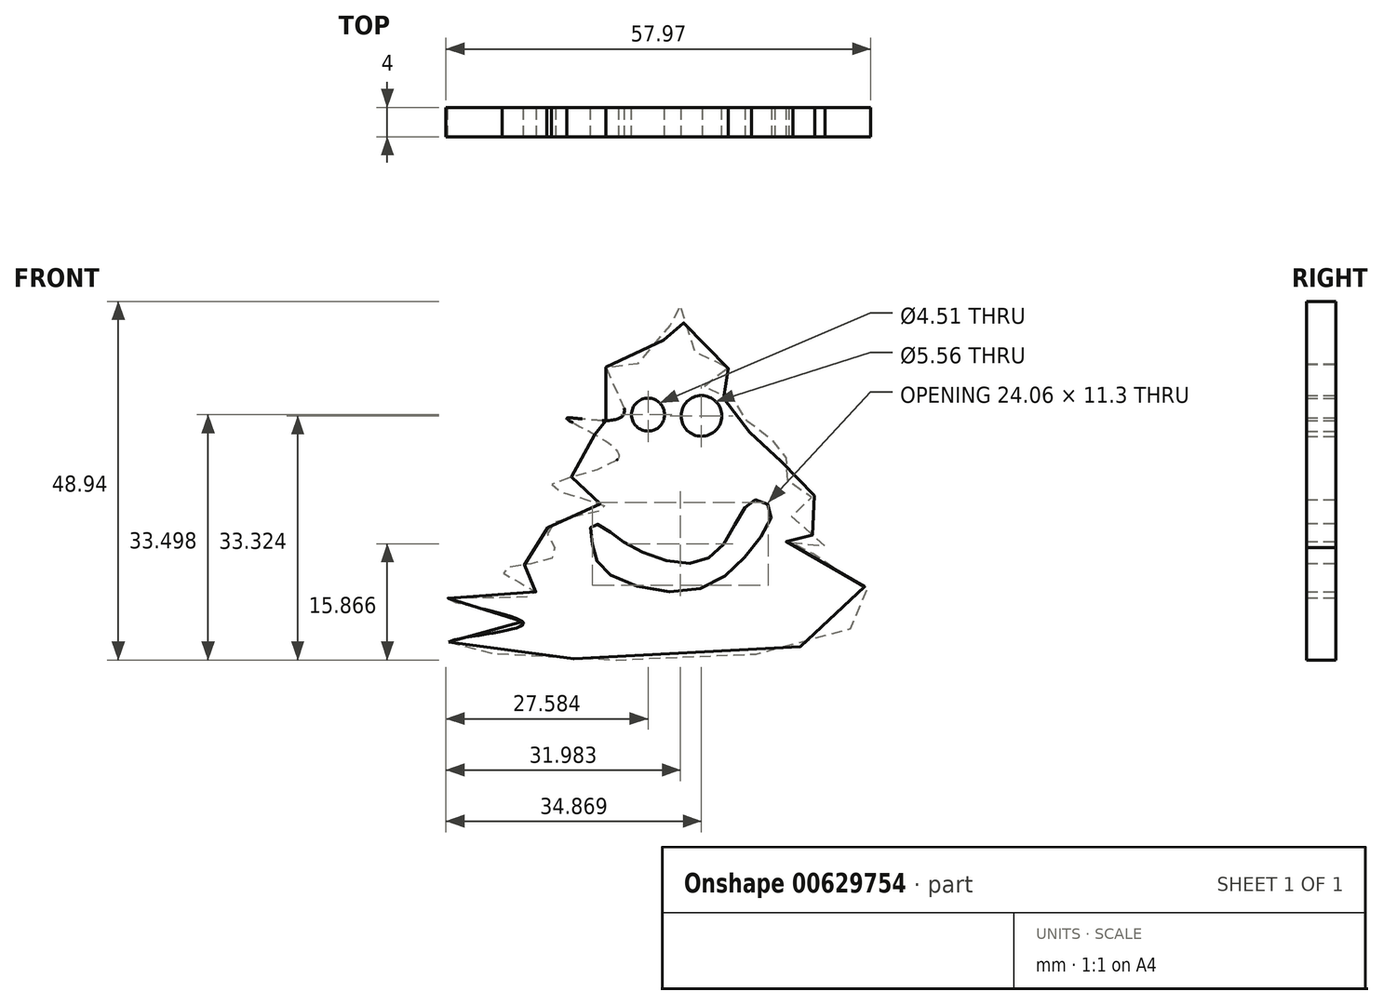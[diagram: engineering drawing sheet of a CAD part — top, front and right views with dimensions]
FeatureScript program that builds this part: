
annotation { "Feature Type Name" : "Feature", "Feature Type Description" : "" }
export const myFeature = defineFeature(function(context is Context, id is Id, definition is map)
    precondition{}
    {
        {
            var Q0;
            Q0=qCreatedBy(makeId("Front.planeOp"),FACE);
            var sketch = newSketch(context, id + "F0", { "sketchPlane" : qUnion([Q0])});
            skFitSpline(sketch, "E0", {"points": [v(-21.5, -34.43) * mm, v(27.06, -34.95) * mm, v(35.21, -26.8) * mm, v(24.63, -20.73) * mm, v(29.83, -21.42) * mm, v(24.98, -16.4) * mm, v(28.45, -14.31) * mm, v(23.07, -11.01) * mm, v(25.5, -8.24) * mm, v(19.08, -5.3) * mm, v(19.77, -2.52) * mm, v(13.18, 0) * mm, v(16.65, 2.86) * mm, v(12.49, 4.77) * mm, v(9.89, 12.06) * mm, v(5.72, 4.08) * mm, v(0, 3.2) * mm, v(2.25, -3.56) * mm, v(-5.38, -3.9) * mm, v(1.73, -9.1) * mm, v(-7.46, -13.1) * mm, v(0, -16.04) * mm, v(-7.98, -18.82) * mm, v(-6.94, -22.64) * mm, v(-14.22, -24.72) * mm, v(-9.54, -27.84) * mm, v(-21.86, -28.53) * mm, v(-11.27, -31.83) * mm, v(-21.5, -34.43) * mm]});
            skCircle(sketch, "E1", {"center": v(5.72, -3.38) * mm, "radius": 2.25 * mm});
            skCircle(sketch, "E2", {"center": v(13, -3.56) * mm, "radius": 2.78 * mm});
            skFitSpline(sketch, "E3", {"points": [v(-1.9, -21.08) * mm, v(0, -24.9) * mm, v(11.97, -27.32) * mm, v(19.95, -21.6) * mm, v(22.55, -16.4) * mm, v(20.64, -15) * mm, v(18.73, -16.4) * mm, v(15.44, -21.77) * mm, v(10.58, -23.68) * mm, v(3.12, -21.25) * mm, v(0, -19) * mm, v(-1.9, -18.3) * mm, v(-1.9, -21.08) * mm]});
            skSolve(sketch);
        }
        {
            var Q0;
            Q0=makeQuery(id+"F0.imprint","IMPRINT",FACE,{"disambiguationData":[TD([[makeQuery(id+"F0.imprint","IMPRINT",EDGE,{"derivedFrom":sQuery(id+"F0.wireOp",EDGE,"E0")}),1.0]])]});
            extrude(context, id + "F1", {"entities" : qUnion([Q0]), "depth" : 4 * mm, "offsetDistance" : 25 * mm});
        }
    });
